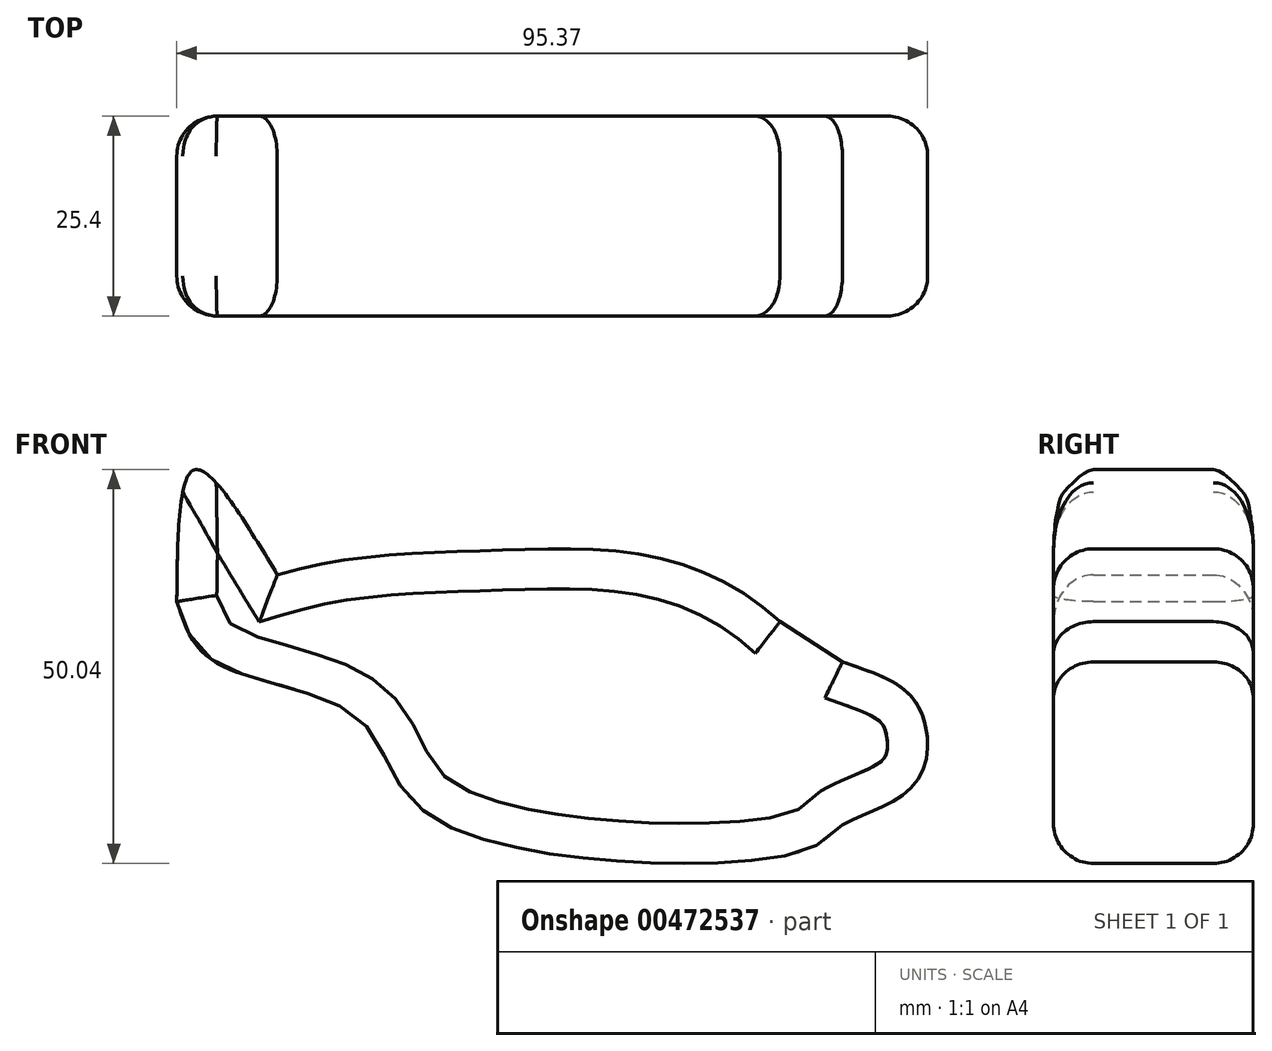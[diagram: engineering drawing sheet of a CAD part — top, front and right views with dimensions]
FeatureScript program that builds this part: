
annotation { "Feature Type Name" : "Feature", "Feature Type Description" : "" }
export const myFeature = defineFeature(function(context is Context, id is Id, definition is map)
    precondition{}
    {
        {
            var Q0;
            Q0=qCreatedBy(makeId("Front.planeOp"),FACE);
            var sketch = newSketch(context, id + "F0", { "sketchPlane" : qUnion([Q0])});
            skFitSpline(sketch, "E0", {"points": [v(-63.84, 50.79) * mm, v(-35.47, 53.9) * mm, v(0, 44.83) * mm], "startDerivative": vector(57.26, 17.49) * mm, "endDerivative": vector(62.5, -57.7) * mm});
            skFitSpline(sketch, "E1", {"points": [v(-76.6, 47.38) * mm, v(-74.34, 64.12) * mm, v(-63.84, 50.79) * mm], "startDerivative": vector(0.44, 48.54) * mm, "endDerivative": vector(25.08, -41.7) * mm});
            skLineSegment(sketch, "E2", {"start": v(0, 44.83) * mm, "end": v(7.94, 39.72) * mm});
            skFitSpline(sketch, "E3", {"points": [v(7.94, 39.72) * mm, v(17.6, 34.05) * mm, v(17.3, 24.4) * mm, v(7.94, 19) * mm, v(2.84, 15.6) * mm, v(-43.98, 19.86) * mm, v(-53.62, 32.63) * mm, v(-71.78, 39.72) * mm, v(-76.6, 47.38) * mm], "startDerivative": vector(142.98, -49.28) * mm, "endDerivative": vector(-30.07, 90.17) * mm});
            skFitSpline(sketch, "E4", {"points": [v(0, 44.83) * mm, v(7.94, 29.8) * mm, v(7.94, 19) * mm], "startDerivative": vector(18.14, -27.11) * mm, "endDerivative": vector(-2.9, -19.55) * mm});
            skSolve(sketch);
        }
        {
            var Q0;
            Q0 = qSketchRegion(id + "F0", true);
            extrude(context, id + "F1", {"entities" : qUnion([Q0]), "depth" : 25.4 * mm});
        }
        {
            var Q0;
            Q0=makeQuery(id+"F1.opExtrude","CAP_FACE",FACE,{"disambiguationData":[OSD([sQuery(id+"F0.wireOp",EDGE,"E0"),sQuery(id+"F0.wireOp",EDGE,"E1"),sQuery(id+"F0.wireOp",EDGE,"E2"),sQuery(id+"F0.wireOp",EDGE,"E3")])],"isStart":false});
            fillet(context, id + "F2", {"entities" : qUnion([Q0]), "radius" : 5.08 * mm, "tangentPropagation" : true, "allowEdgeOverflow" : false});
        }
        {
            var Q0;
            Q0=makeQuery(id+"F1.opExtrude","CAP_FACE",FACE,{"disambiguationData":[OSD([sQuery(id+"F0.wireOp",EDGE,"E0"),sQuery(id+"F0.wireOp",EDGE,"E1"),sQuery(id+"F0.wireOp",EDGE,"E2"),sQuery(id+"F0.wireOp",EDGE,"E3")])],"isStart":true});
            fillet(context, id + "F3", {"entities" : qUnion([Q0]), "radius" : 5.08 * mm, "tangentPropagation" : true, "allowEdgeOverflow" : false});
        }
    });
